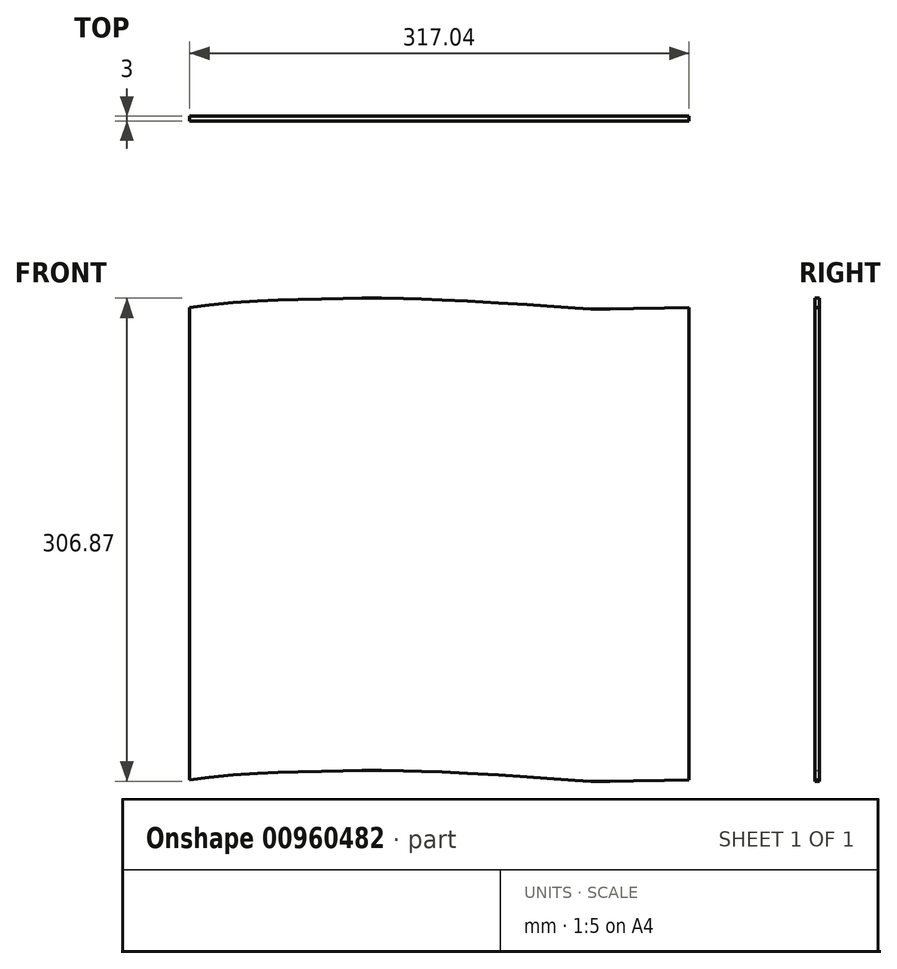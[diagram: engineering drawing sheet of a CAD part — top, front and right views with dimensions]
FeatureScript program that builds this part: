
annotation { "Feature Type Name" : "Feature", "Feature Type Description" : "" }
export const myFeature = defineFeature(function(context is Context, id is Id, definition is map)
    precondition{}
    {
        {
            var Q0;
            Q0=qCreatedBy(makeId("Front.planeOp"),FACE);
            var sketch = newSketch(context, id + "F0", { "sketchPlane" : qUnion([Q0])});
            skFitSpline(sketch, "E0.0", {"points": [v(-0.2, 1.49) * mm, v(7.68, 2.57) * mm, v(24.97, 4.95) * mm, v(59.14, 6.64) * mm, v(109.61, 7.62) * mm, v(145.3, 7.79) * mm, v(234.5, 2.42) * mm, v(252.69, 0.21) * mm, v(291.99, 1.09) * mm, v(317, 1.64) * mm], "construction": true});
            skFitSpline(sketch, "E1.0", {"points": [v(0, 0) * mm, v(2.28, 0.31) * mm, v(6.85, 0.94) * mm, v(13.79, 1.84) * mm, v(20.94, 2.66) * mm, v(28.4, 3.35) * mm, v(36.29, 3.91) * mm, v(43.27, 4.3) * mm, v(49.14, 4.56) * mm, v(53.7, 4.74) * mm, v(58.4, 4.9) * mm, v(63.3, 5.06) * mm, v(68.3, 5.2) * mm, v(75.12, 5.39) * mm, v(82.02, 5.55) * mm, v(88.86, 5.69) * mm, v(93.9, 5.78) * mm, v(98.83, 5.87) * mm, v(103.6, 5.94) * mm, v(108.14, 6) * mm, v(112.46, 6.06) * mm, v(116.65, 6.1) * mm, v(122.16, 6.12) * mm, v(127.77, 6.09) * mm, v(133.82, 5.99) * mm, v(138.68, 5.87) * mm, v(143.07, 5.74) * mm, v(146.83, 5.6) * mm, v(150.77, 5.45) * mm, v(156.04, 5.23) * mm, v(162.79, 4.92) * mm, v(169.86, 4.57) * mm, v(179.57, 4.07) * mm, v(192, 3.37) * mm, v(204.06, 2.65) * mm, v(213.08, 2.08) * mm, v(219.42, 1.66) * mm, v(224.26, 1.33) * mm, v(227.81, 1.08) * mm, v(230.3, 0.9) * mm, v(232.6, 0.72) * mm, v(234.71, 0.56) * mm, v(236.63, 0.4) * mm, v(239, 0.2) * mm, v(241.65, -0.01) * mm, v(244.57, -0.24) * mm, v(247.43, -0.42) * mm, v(250.45, -0.57) * mm, v(253.84, -0.67) * mm, v(257.8, -0.73) * mm, v(262.27, -0.75) * mm, v(267.2, -0.74) * mm, v(272.53, -0.7) * mm, v(280.12, -0.6) * mm, v(290.38, -0.43) * mm, v(303.5, -0.16) * mm, v(312.53, 0.04) * mm, v(317.04, 0.14) * mm]});
            skFitSpline(sketch, "E2.0", {"points": [v(-0.4, 2.97) * mm, v(1.87, 3.29) * mm, v(6.45, 3.92) * mm, v(13.42, 4.82) * mm, v(20.62, 5.65) * mm, v(28.16, 6.34) * mm, v(36.1, 6.9) * mm, v(43.12, 7.29) * mm, v(49.02, 7.55) * mm, v(53.58, 7.74) * mm, v(58.3, 7.9) * mm, v(63.2, 8.06) * mm, v(68.22, 8.2) * mm, v(75.04, 8.39) * mm, v(81.96, 8.55) * mm, v(88.8, 8.69) * mm, v(93.85, 8.78) * mm, v(98.78, 8.87) * mm, v(103.55, 8.94) * mm, v(108.1, 9) * mm, v(112.43, 9.06) * mm, v(116.63, 9.1) * mm, v(122.16, 9.12) * mm, v(127.8, 9.09) * mm, v(133.89, 8.99) * mm, v(138.77, 8.87) * mm, v(143.17, 8.74) * mm, v(146.94, 8.6) * mm, v(150.9, 8.45) * mm, v(156.17, 8.23) * mm, v(162.93, 7.92) * mm, v(170, 7.57) * mm, v(179.74, 7.06) * mm, v(192.16, 6.37) * mm, v(204.24, 5.64) * mm, v(213.27, 5.07) * mm, v(219.62, 4.65) * mm, v(224.47, 4.32) * mm, v(228.03, 4.07) * mm, v(230.52, 3.89) * mm, v(232.84, 3.71) * mm, v(234.95, 3.55) * mm, v(236.88, 3.4) * mm, v(239.25, 3.2) * mm, v(241.9, 2.98) * mm, v(244.78, 2.75) * mm, v(247.6, 2.57) * mm, v(250.56, 2.43) * mm, v(253.9, 2.33) * mm, v(257.83, 2.27) * mm, v(262.27, 2.25) * mm, v(267.18, 2.26) * mm, v(272.5, 2.3) * mm, v(280.08, 2.4) * mm, v(290.32, 2.57) * mm, v(303.44, 2.84) * mm, v(312.46, 3.04) * mm, v(316.97, 3.14) * mm]});
            skLineSegment(sketch, "E3", {"start": v(-0.4, 2.97) * mm, "end": v(0, 0) * mm});
            skLineSegment(sketch, "E4", {"start": v(316.97, 3.14) * mm, "end": v(317.04, 0.14) * mm});
            skLineSegment(sketch, "E5", {"start": v(0, 0) * mm, "end": v(0, -300) * mm});
            skLineSegment(sketch, "E6", {"start": v(317.04, 0.14) * mm, "end": v(317.04, -299.86) * mm});
            skFitSpline(sketch, "E7.0", {"points": [v(0, -300) * mm, v(2.28, -299.69) * mm, v(6.85, -299.06) * mm, v(13.79, -298.16) * mm, v(20.94, -297.34) * mm, v(28.4, -296.65) * mm, v(36.29, -296.09) * mm, v(43.27, -295.7) * mm, v(49.14, -295.44) * mm, v(53.7, -295.26) * mm, v(58.4, -295.1) * mm, v(63.3, -294.94) * mm, v(68.3, -294.8) * mm, v(75.12, -294.61) * mm, v(82.02, -294.45) * mm, v(88.86, -294.31) * mm, v(93.9, -294.22) * mm, v(98.83, -294.13) * mm, v(103.6, -294.06) * mm, v(108.14, -294) * mm, v(112.46, -293.94) * mm, v(116.65, -293.9) * mm, v(122.16, -293.88) * mm, v(127.77, -293.91) * mm, v(133.82, -294.01) * mm, v(138.68, -294.13) * mm, v(143.07, -294.26) * mm, v(146.83, -294.4) * mm, v(150.77, -294.55) * mm, v(156.04, -294.77) * mm, v(162.79, -295.08) * mm, v(169.86, -295.43) * mm, v(179.57, -295.93) * mm, v(192, -296.63) * mm, v(204.06, -297.35) * mm, v(213.08, -297.92) * mm, v(219.42, -298.34) * mm, v(224.26, -298.67) * mm, v(227.81, -298.92) * mm, v(230.3, -299.1) * mm, v(232.6, -299.28) * mm, v(234.71, -299.44) * mm, v(236.63, -299.6) * mm, v(239, -299.8) * mm, v(241.65, -300.01) * mm, v(244.57, -300.24) * mm, v(247.43, -300.42) * mm, v(250.45, -300.57) * mm, v(253.84, -300.67) * mm, v(257.8, -300.73) * mm, v(262.27, -300.75) * mm, v(267.2, -300.74) * mm, v(272.53, -300.7) * mm, v(280.12, -300.6) * mm, v(290.38, -300.43) * mm, v(303.5, -300.16) * mm, v(312.53, -299.96) * mm, v(317.04, -299.86) * mm]});
            skSolve(sketch);
        }
        {
            var Q0;
            Q0=makeQuery(id+"F0.imprint","IMPRINT",FACE,{"disambiguationData":[TD([[makeQuery(id+"F0.imprint","IMPRINT",EDGE,{"derivedFrom":sQuery(id+"F0.wireOp",EDGE,"E1.0")}),-1.0]])]});
            extrude(context, id + "F1", {"entities" : qUnion([Q0]), "depth" : 3 * mm, "offsetDistance" : 25 * mm});
        }
    });
